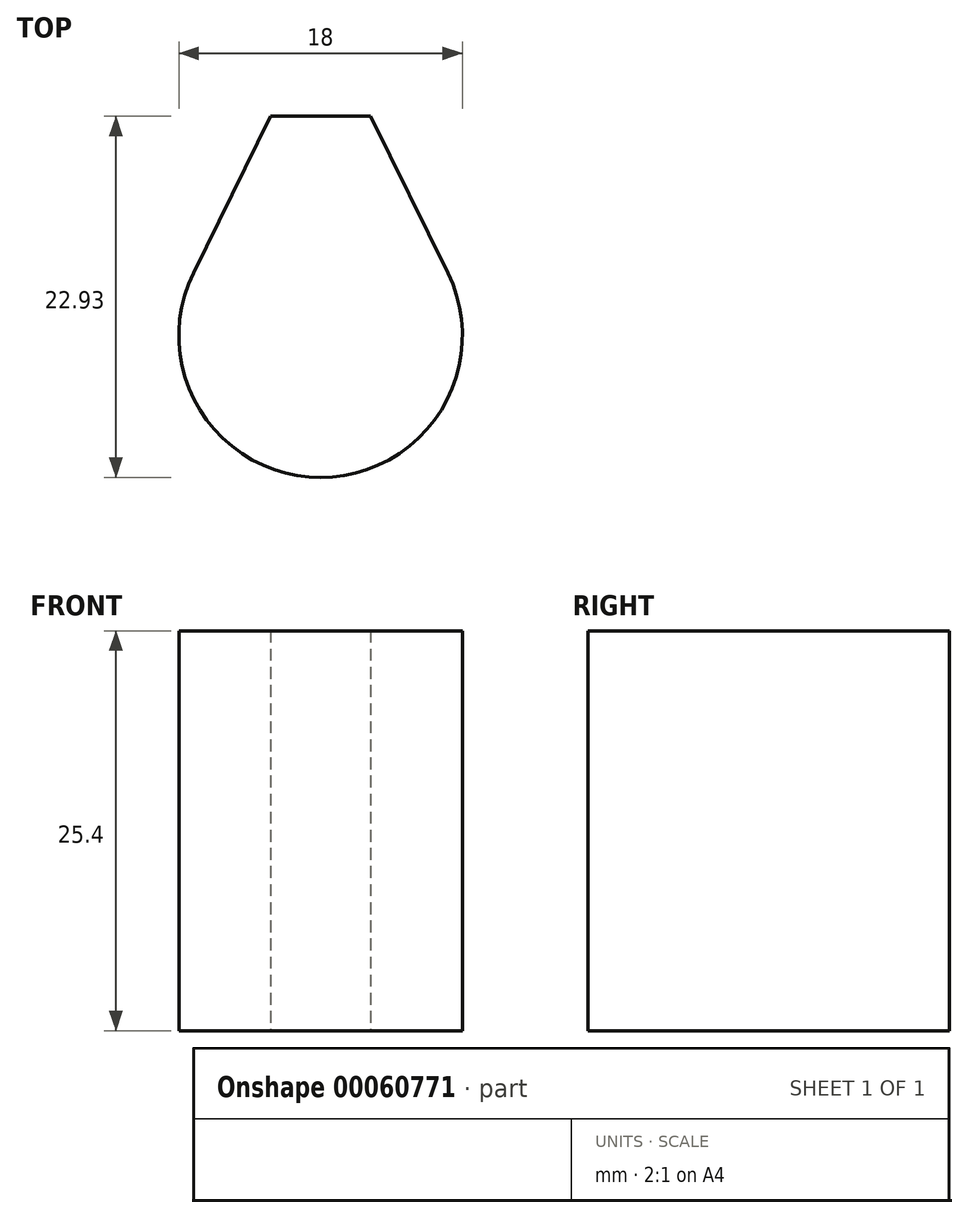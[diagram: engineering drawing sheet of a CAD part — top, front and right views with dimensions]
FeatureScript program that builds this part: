
annotation { "Feature Type Name" : "Feature", "Feature Type Description" : "" }
export const myFeature = defineFeature(function(context is Context, id is Id, definition is map)
    precondition{}
    {
        {
            var Q0;
            Q0=qCreatedBy(makeId("Top.planeOp"),FACE);
            var sketch = newSketch(context, id + "F0", { "sketchPlane" : qUnion([Q0])});
            skArc(sketch, "E0", {"start": v(-8.08, 3.98) * mm, "mid": v(0, -9) * mm, "end": v(8.08, 3.98) * mm});
            skCircle(sketch, "E1", {"center": v(0, 0) * mm, "radius": 6.35 * mm});
            skLineSegment(sketch, "E2", {"start": v(3.21, 13.86) * mm, "end": v(-3.21, 13.86) * mm});
            skLineSegment(sketch, "E3", {"start": v(3.17, 13.93) * mm, "end": v(3.17, 13.86) * mm});
            skLineSegment(sketch, "E4.MirrorCS", {"start": v(-3.17, 13.93) * mm, "end": v(-3.17, 13.86) * mm});
            skLineSegment(sketch, "E5", {"start": v(8.08, 3.98) * mm, "end": v(3.17, 13.93) * mm});
            skLineSegment(sketch, "E6", {"start": v(3.17, 13.93) * mm, "end": v(-3.17, 13.93) * mm});
            skLineSegment(sketch, "E7", {"start": v(-3.17, 13.93) * mm, "end": v(-8.08, 3.98) * mm});
            skPoint(sketch, "E8.orphan", {"position": v(-3.17, 25.13) * mm});
            skPoint(sketch, "E9.orphan", {"position": v(-11.01, 13.86) * mm});
            skPoint(sketch, "E10.orphan", {"position": v(3.17, 25.13) * mm});
            skPoint(sketch, "E11.orphan", {"position": v(-3.17, 11.27) * mm});
            skPoint(sketch, "E12.orphan", {"position": v(3.17, 11.27) * mm});
            skSolve(sketch);
        }
        {
            var Q0;
            Q0 = qSketchRegion(id + "F0", true);
            var Q1;
            Q1=makeQuery(id+"F0.imprint","IMPRINT",FACE,{"disambiguationData":[TD([[makeQuery(id+"F0.imprint","IMPRINT",EDGE,{"derivedFrom":sQuery(id+"F0.wireOp",EDGE,"E1")}),1.0]])]});
            extrude(context, id + "F1", {"entities" : qUnion([Q0, Q1]), "depth" : 25.4 * mm});
        }
    });
